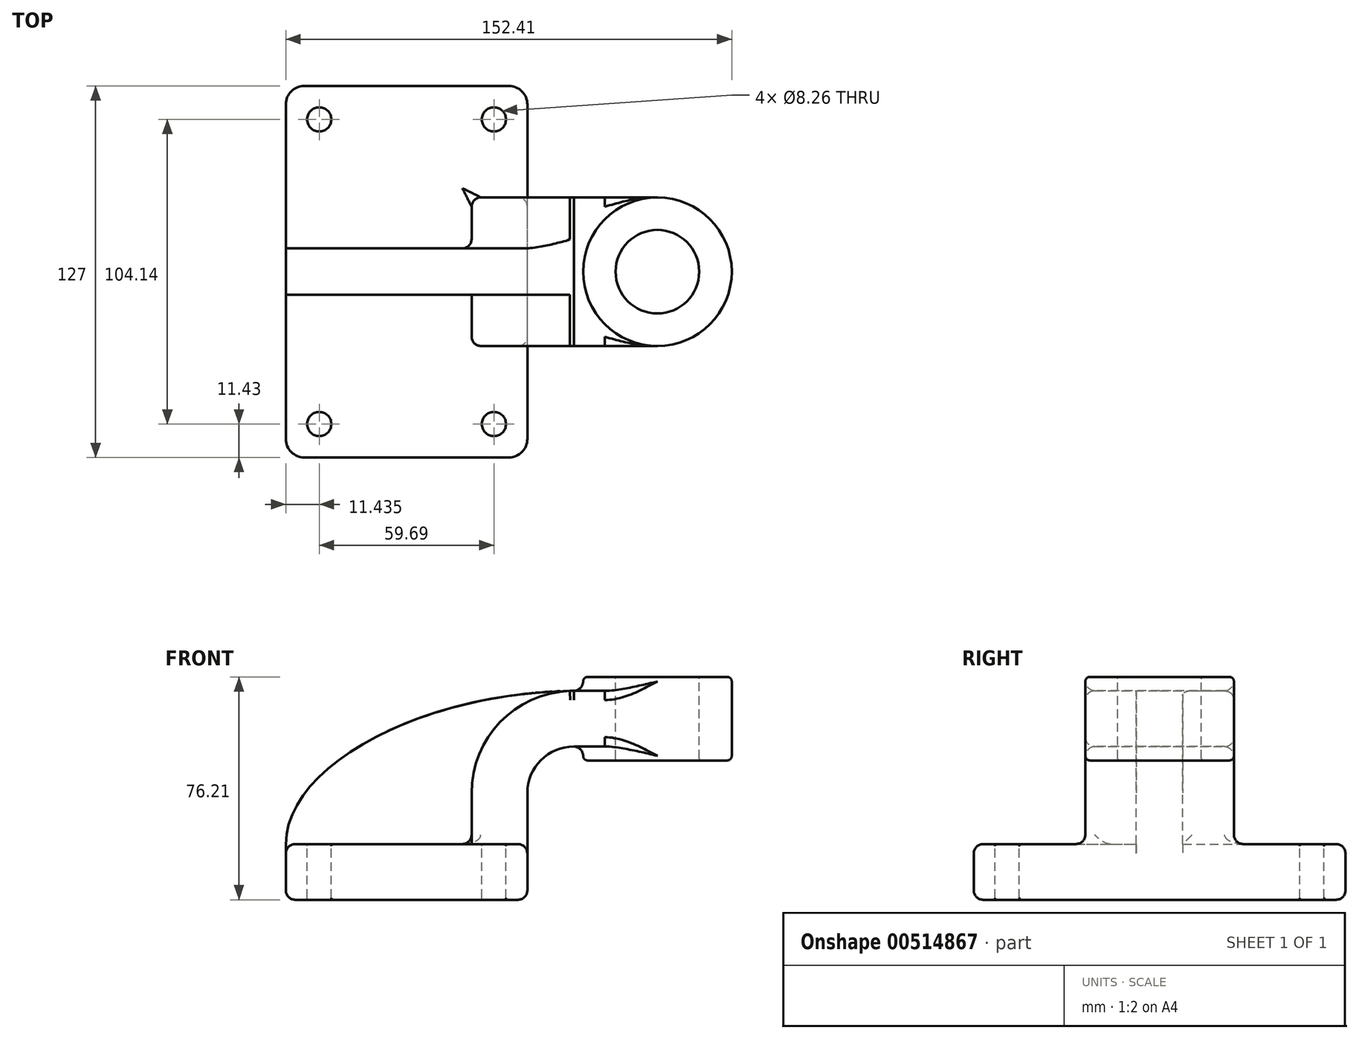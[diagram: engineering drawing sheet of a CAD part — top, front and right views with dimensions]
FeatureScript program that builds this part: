
annotation { "Feature Type Name" : "Feature", "Feature Type Description" : "" }
export const myFeature = defineFeature(function(context is Context, id is Id, definition is map)
    precondition{}
    {
        {
            var Q0;
            Q0=qCreatedBy(makeId("Front.planeOp"),FACE);
            var sketch = newSketch(context, id + "F0", { "sketchPlane" : qUnion([Q0])});
            skLineSegment(sketch, "E0.bottom", {"start": v(41.27, 9.53) * mm, "end": v(-41.28, 9.53) * mm});
            skLineSegment(sketch, "E0.top", {"start": v(41.28, -9.52) * mm, "end": v(-41.27, -9.52) * mm});
            skLineSegment(sketch, "E0.left", {"start": v(41.28, 9.53) * mm, "end": v(41.28, -9.52) * mm});
            skLineSegment(sketch, "E0.right", {"start": v(-41.28, 9.53) * mm, "end": v(-41.27, -9.52) * mm});
            skPoint(sketch, "E0.middle", {"position": v(0, 0) * mm});
            skLineSegment(sketch, "E1.bottom", {"start": v(60.32, 66.68) * mm, "end": v(111.12, 66.68) * mm});
            skLineSegment(sketch, "E1.top", {"start": v(60.33, 38.1) * mm, "end": v(111.12, 38.1) * mm});
            skLineSegment(sketch, "E1.left", {"start": v(60.32, 66.68) * mm, "end": v(60.33, 38.1) * mm});
            skLineSegment(sketch, "E1.right", {"start": v(111.12, 66.68) * mm, "end": v(111.12, 38.1) * mm});
            skPoint(sketch, "E1.middle", {"position": v(85.72, 52.39) * mm});
            skLineSegment(sketch, "E2", {"start": v(41.27, 9.53) * mm, "end": v(41.27, 26.99) * mm});
            skArc(sketch, "E3", {"start": v(41.27, 26.99) * mm, "mid": v(45.92, 38.21) * mm, "end": v(57.15, 42.86) * mm});
            skLineSegment(sketch, "E4", {"start": v(57.15, 42.86) * mm, "end": v(85.72, 42.86) * mm});
            skLineSegment(sketch, "E5.0", {"start": v(57.15, 61.91) * mm, "end": v(85.72, 61.91) * mm});
            skArc(sketch, "E5.1", {"start": v(22.22, 26.99) * mm, "mid": v(32.45, 51.68) * mm, "end": v(57.15, 61.91) * mm});
            skLineSegment(sketch, "E5.2", {"start": v(22.22, 9.53) * mm, "end": v(22.22, 26.99) * mm});
            skLineSegment(sketch, "E6", {"start": v(85.72, 38.1) * mm, "end": v(85.72, 66.68) * mm});
            skFitSpline(sketch, "E7", {"points": [v(-41.28, 9.53) * mm, v(57.15, 61.91) * mm], "startDerivative": vector(0.01, 78.26) * mm, "endDerivative": vector(161.16, 2.45) * mm});
            skSolve(sketch);
        }
        {
            var Q0;
            Q0=makeQuery(id+"F0.imprint","IMPRINT",FACE,{"disambiguationData":[TD([[makeQuery(id+"F0.imprint","IMPRINT",EDGE,{"derivedFrom":sQuery(id+"F0.wireOp",EDGE,"E0.top")}),-1.0]])]});
            extrude(context, id + "F1", {"entities" : qUnion([Q0]), "endBound" : BoundingType.SYMMETRIC, "depth" : 127 * mm});
        }
        {
            var Q0;
            {var subQ3=sQuery(id+"F0.wireOp",EDGE,"E5.2");Q0=makeQuery(id+"F0.imprint","IMPRINT",FACE,{"disambiguationData":[TD([[makeQuery(id+"F0.imprint","IMPRINT",EDGE,{"derivedFrom":subQ3}),1.0]])]});}
            extrude(context, id + "F2", {"entities" : qUnion([Q0]), "operationType" : NewBodyOperationType.ADD, "endBound" : BoundingType.SYMMETRIC, "depth" : 15.88 * mm});
        }
        {
            var Q0;
            {var subQ1=sQuery(id+"F0.wireOp",EDGE,"E2");Q0=makeQuery(id+"F0.imprint","IMPRINT",FACE,{"disambiguationData":[TD([[makeQuery(id+"F0.imprint","IMPRINT",EDGE,{"derivedFrom":subQ1}),1.0]])]});}
            var Q1;
            {var subQ0=sQuery(id+"F0.wireOp",EDGE,"E5.0");var subQ1=sQuery(id+"F0.wireOp",EDGE,"E1.left");var subQ2=makeQuery(id+"F0.imprint","INTERSECT",VERTEX,{"derivedFrom":[subQ1,subQ0]});Q1=makeQuery(id+"F0.imprint","IMPRINT",FACE,{"disambiguationData":[TD([[makeQuery(id+"F0.imprint","IMPRINT",EDGE,{"disambiguationData":[TD([[subQ2,-1.0]])],"derivedFrom":subQ1}),1.0]])]});}
            extrude(context, id + "F3", {"entities" : qUnion([Q0, Q1]), "operationType" : NewBodyOperationType.ADD, "endBound" : BoundingType.SYMMETRIC, "depth" : 50.8 * mm});
        }
        {
            var Q0;
            {var subQ4=sQuery(id+"F0.wireOp",EDGE,"E1.right");Q0=makeQuery(id+"F0.imprint","IMPRINT",FACE,{"disambiguationData":[TD([[makeQuery(id+"F0.imprint","IMPRINT",EDGE,{"derivedFrom":subQ4}),-1.0]])]});}
            var Q1;
            Q1=sQuery(id+"F0.wireOp",EDGE,"E6");
            revolve(context, id + "F4", {"operationType" : NewBodyOperationType.ADD, "entities" : qUnion([Q0]), "axis" : qUnion([Q1]), "revolveType" : RevolveType.FULL});
        }
        {
            var Q0;
            Q0=makeQuery(id+"F1.opExtrude","CAP_EDGE",EDGE,{"disambiguationData":[OSD([sQuery(id+"F0.wireOp",EDGE,"E0.left")])],"isStart":true});
            var Q1;
            Q1=makeQuery(id+"F1.opExtrude","CAP_EDGE",EDGE,{"disambiguationData":[OSD([sQuery(id+"F0.wireOp",EDGE,"E0.right")])],"isStart":true});
            var Q2;
            Q2=makeQuery(id+"F1.opExtrude","CAP_EDGE",EDGE,{"disambiguationData":[OSD([sQuery(id+"F0.wireOp",EDGE,"E0.right")])],"isStart":false});
            var Q3;
            Q3=makeQuery(id+"F1.opExtrude","CAP_EDGE",EDGE,{"disambiguationData":[OSD([sQuery(id+"F0.wireOp",EDGE,"E0.left")])],"isStart":false});
            fillet(context, id + "F5", {"entities" : qUnion([Q0, Q1, Q2, Q3]), "radius" : 6.35 * mm, "tangentPropagation" : true, "allowEdgeOverflow" : false});
        }
        {
            var Q0;
            Q0=makeQuery(id+"F4.boolean.opBoolean","INTERSECT",EDGE,{"derivedFrom":[makeQuery(id+"F3.opExtrude","SWEPT_FACE",FACE,{"disambiguationData":[OSD([sQuery(id+"F0.wireOp",EDGE,"E5.0")])]}),makeQuery(id+"F4.opRevolve","SWEPT_FACE",FACE,{"disambiguationData":[OSD([sQuery(id+"F0.wireOp",EDGE,"E1.right")])]})]});
            var Q1;
            Q1=makeQuery(id+"F4.boolean.opBoolean","INTERSECT",EDGE,{"derivedFrom":[makeQuery(id+"F3.opExtrude","SWEPT_FACE",FACE,{"disambiguationData":[OSD([sQuery(id+"F0.wireOp",EDGE,"E4")])]}),makeQuery(id+"F4.opRevolve","SWEPT_FACE",FACE,{"disambiguationData":[OSD([sQuery(id+"F0.wireOp",EDGE,"E1.right")])]})]});
            var Q2;
            Q2=makeQuery(id+"F2.opExtrude","CAP_EDGE",EDGE,{"disambiguationData":[OSD([sQuery(id+"F0.wireOp",EDGE,"E5.1")])],"isStart":true});
            var Q3;
            Q3=makeQuery(id+"F2.opExtrude","CAP_EDGE",EDGE,{"disambiguationData":[OSD([sQuery(id+"F0.wireOp",EDGE,"E5.1")])],"isStart":false});
            var Q4;
            {var subQ0=sQuery(id+"F0.wireOp",EDGE,"E0.bottom");var subQ1=sQuery(id+"F0.wireOp",EDGE,"E7");var subQ2=sQuery(id+"F0.wireOp",EDGE,"E5.2");var subQ3=sQuery(id+"F0.wireOp",EDGE,"E5.1");Q4=makeQuery(id+"F3.boolean.opBoolean","SPLIT",EDGE,{"disambiguationData":[TD([makeQuery(id+"F2.opExtrude","CAP_FACE",FACE,{"disambiguationData":[OSD([subQ0,subQ3,subQ2,subQ1])],"isStart":false})])],"derivedFrom":makeQuery(id+"F3.opExtrude","SWEPT_EDGE",EDGE,{"disambiguationData":[OSD([subQ0,subQ2])]})});}
            var Q5;
            Q5=makeQuery(id+"F2.opExtrude","CAP_EDGE",EDGE,{"disambiguationData":[OSD([sQuery(id+"F0.wireOp",EDGE,"E0.bottom")])],"isStart":false});
            var Q6;
            Q6=makeQuery(id+"F3.opExtrude","CAP_EDGE",EDGE,{"disambiguationData":[OSD([sQuery(id+"F0.wireOp",EDGE,"E0.bottom")])],"isStart":false});
            var Q7;
            Q7=makeQuery(id+"F3.opExtrude","CAP_EDGE",EDGE,{"disambiguationData":[OSD([sQuery(id+"F0.wireOp",EDGE,"E0.bottom")])],"isStart":true});
            var Q8;
            {var subQ0=sQuery(id+"F0.wireOp",EDGE,"E0.bottom");var subQ1=sQuery(id+"F0.wireOp",EDGE,"E7");var subQ2=sQuery(id+"F0.wireOp",EDGE,"E5.2");var subQ3=sQuery(id+"F0.wireOp",EDGE,"E5.1");Q8=makeQuery(id+"F3.boolean.opBoolean","SPLIT",EDGE,{"disambiguationData":[TD([makeQuery(id+"F2.opExtrude","CAP_FACE",FACE,{"disambiguationData":[OSD([subQ0,subQ3,subQ2,subQ1])],"isStart":true})])],"derivedFrom":makeQuery(id+"F3.opExtrude","SWEPT_EDGE",EDGE,{"disambiguationData":[OSD([subQ0,subQ2])]})});}
            var Q9;
            Q9=makeQuery(id+"F2.opExtrude","CAP_EDGE",EDGE,{"disambiguationData":[OSD([sQuery(id+"F0.wireOp",EDGE,"E0.bottom")])],"isStart":true});
            fillet(context, id + "F6", {"entities" : qUnion([Q0, Q1, Q2, Q3, Q4, Q5, Q6, Q7, Q8, Q9]), "radius" : 3.17 * mm, "tangentPropagation" : true, "allowEdgeOverflow" : false});
        }
        {
            var Q0;
            Q0=makeQuery(id+"F4.opRevolve","SWEPT_EDGE",EDGE,{"disambiguationData":[OSD([sQuery(id+"F0.wireOp",EDGE,"E1.bottom"),sQuery(id+"F0.wireOp",EDGE,"E1.right")])]});
            var Q1;
            Q1=makeQuery(id+"F4.opRevolve","SWEPT_EDGE",EDGE,{"disambiguationData":[OSD([sQuery(id+"F0.wireOp",EDGE,"E1.top"),sQuery(id+"F0.wireOp",EDGE,"E1.right")])]});
            fillet(context, id + "F7", {"entities" : qUnion([Q0, Q1]), "radius" : 1.59 * mm, "tangentPropagation" : true, "allowEdgeOverflow" : false});
        }
        {
            var Q0;
            Q0=makeQuery(id+"F3.opExtrude","CAP_FACE",FACE,{"disambiguationData":[OSD([sQuery(id+"F0.wireOp",EDGE,"E0.bottom"),sQuery(id+"F0.wireOp",EDGE,"E2"),sQuery(id+"F0.wireOp",EDGE,"E3"),sQuery(id+"F0.wireOp",EDGE,"E4"),sQuery(id+"F0.wireOp",EDGE,"E5.0"),sQuery(id+"F0.wireOp",EDGE,"E5.1"),sQuery(id+"F0.wireOp",EDGE,"E5.2"),sQuery(id+"F0.wireOp",EDGE,"E6"),sQuery(id+"F0.wireOp",EDGE,"E7")])],"isStart":true});
            var Q1;
            Q1=makeQuery(id+"F3.opExtrude","CAP_FACE",FACE,{"disambiguationData":[OSD([sQuery(id+"F0.wireOp",EDGE,"E0.bottom"),sQuery(id+"F0.wireOp",EDGE,"E2"),sQuery(id+"F0.wireOp",EDGE,"E3"),sQuery(id+"F0.wireOp",EDGE,"E4"),sQuery(id+"F0.wireOp",EDGE,"E5.0"),sQuery(id+"F0.wireOp",EDGE,"E5.1"),sQuery(id+"F0.wireOp",EDGE,"E5.2"),sQuery(id+"F0.wireOp",EDGE,"E6"),sQuery(id+"F0.wireOp",EDGE,"E7")])],"isStart":false});
            var Q2;
            Q2=makeQuery(id+"F1.opExtrude","SWEPT_FACE",FACE,{"disambiguationData":[OSD([sQuery(id+"F0.wireOp",EDGE,"E0.top")])]});
            fillet(context, id + "F8", {"entities" : qUnion([Q0, Q1, Q2]), "radius" : 3.17 * mm, "tangentPropagation" : true, "allowEdgeOverflow" : false});
        }
        {
            var Q0;
            Q0=makeQuery(id+"F4.opRevolve","SWEPT_FACE",FACE,{"disambiguationData":[OSD([sQuery(id+"F0.wireOp",EDGE,"E1.bottom")])]});
            var sketch = newSketch(context, id + "F9", { "sketchPlane" : qUnion([Q0])});
            skCircle(sketch, "E8", {"center": v(85.72, 0) * mm, "radius": 14.29 * mm});
            skSolve(sketch);
        }
        {
            var Q0;
            Q0 = qSketchRegion(id + "F9", true);
            extrude(context, id + "F10", {"entities" : qUnion([Q0]), "operationType" : NewBodyOperationType.REMOVE, "endBound" : BoundingType.THROUGH_ALL, "oppositeDirection" : true, "depth" : 25.4 * mm});
        }
        {
            var Q0;
            {var subQ3=sQuery(id+"F0.wireOp",EDGE,"E0.bottom");var subQ4=sQuery(id+"F0.wireOp",EDGE,"E0.right");var subQ5=sQuery(id+"F0.wireOp",EDGE,"E0.left");Q0=makeQuery(id+"F3.boolean.opBoolean","SPLIT",FACE,{"disambiguationData":[TD([makeQuery(id+"F1.opExtrude","CAP_FACE",FACE,{"disambiguationData":[OSD([subQ3,sQuery(id+"F0.wireOp",EDGE,"E0.top"),subQ5,subQ4])],"isStart":true})])],"derivedFrom":makeQuery(id+"F1.opExtrude","SWEPT_FACE",FACE,{"disambiguationData":[OSD([subQ3])]})});}
            var sketch = newSketch(context, id + "F11", { "sketchPlane" : qUnion([Q0])});
            skCircle(sketch, "E9", {"center": v(-29.85, 52.07) * mm, "radius": 4.13 * mm});
            skCircle(sketch, "E10", {"center": v(29.85, 52.07) * mm, "radius": 4.13 * mm});
            skCircle(sketch, "E11", {"center": v(-29.85, -52.07) * mm, "radius": 4.13 * mm});
            skCircle(sketch, "E12", {"center": v(29.85, -52.07) * mm, "radius": 4.13 * mm});
            skSolve(sketch);
        }
        {
            var Q0;
            Q0 = qSketchRegion(id + "F11", true);
            extrude(context, id + "F12", {"entities" : qUnion([Q0]), "operationType" : NewBodyOperationType.REMOVE, "endBound" : BoundingType.THROUGH_ALL, "oppositeDirection" : true, "depth" : 25.4 * mm});
        }
        {
            var Q0;
            Q0=makeQuery(id+"F12.boolean.opBoolean","COPY",FACE,{"derivedFrom":makeQuery(id+"F12.opExtrude","SWEPT_FACE",FACE,{"disambiguationData":[OSD([sQuery(id+"F11.wireOp",EDGE,"E9")])]})});
            var Q1;
            Q1=makeQuery(id+"F12.boolean.opBoolean","COPY",FACE,{"derivedFrom":makeQuery(id+"F12.opExtrude","SWEPT_FACE",FACE,{"disambiguationData":[OSD([sQuery(id+"F11.wireOp",EDGE,"E10")])]})});
            var Q2;
            Q2=makeQuery(id+"F12.boolean.opBoolean","COPY",FACE,{"derivedFrom":makeQuery(id+"F12.opExtrude","SWEPT_FACE",FACE,{"disambiguationData":[OSD([sQuery(id+"F11.wireOp",EDGE,"E11")])]})});
            var Q3;
            Q3=makeQuery(id+"F12.boolean.opBoolean","COPY",FACE,{"derivedFrom":makeQuery(id+"F12.opExtrude","SWEPT_FACE",FACE,{"disambiguationData":[OSD([sQuery(id+"F11.wireOp",EDGE,"E12")])]})});
            var Q4;
            Q4=makeQuery(id+"F10.boolean.opBoolean","COPY",FACE,{"derivedFrom":makeQuery(id+"F10.opExtrude","SWEPT_FACE",FACE,{"disambiguationData":[OSD([sQuery(id+"F9.wireOp",EDGE,"E8")])]})});
            fillet(context, id + "F13", {"entities" : qUnion([Q0, Q1, Q2, Q3, Q4]), "radius" : 0.64 * mm, "tangentPropagation" : true, "allowEdgeOverflow" : false});
        }
    });
